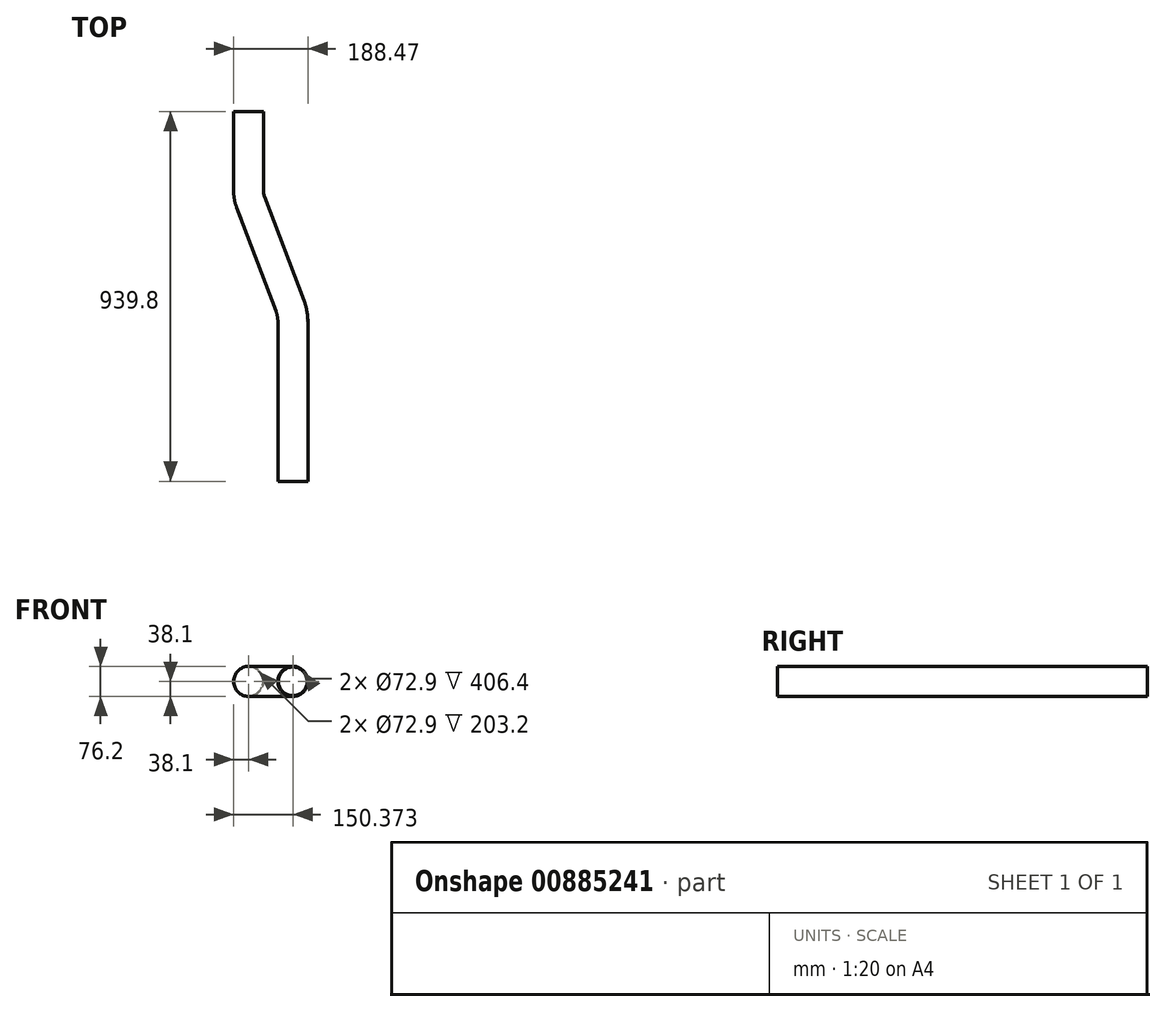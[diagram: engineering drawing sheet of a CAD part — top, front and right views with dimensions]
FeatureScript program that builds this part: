
annotation { "Feature Type Name" : "Feature", "Feature Type Description" : "" }
export const myFeature = defineFeature(function(context is Context, id is Id, definition is map)
    precondition{}
    {
        {
            var Q0;
            Q0=qCreatedBy(makeId("Front.planeOp"),FACE);
            var sketch = newSketch(context, id + "F0", { "sketchPlane" : qUnion([Q0])});
            skCircle(sketch, "E0", {"center": v(0, 0) * mm, "radius": 38.1 * mm});
            skCircle(sketch, "E1", {"center": v(0, 0) * mm, "radius": 36.45 * mm});
            skSolve(sketch);
        }
        {
            var Q0;
            Q0=qCreatedBy(makeId("Top.planeOp"),FACE);
            var sketch = newSketch(context, id + "F1", { "sketchPlane" : qUnion([Q0])});
            skLineSegment(sketch, "E2", {"start": v(0, 0) * mm, "end": v(0, -203.2) * mm});
            skArc(sketch, "E3", {"start": v(0, -203.2) * mm, "mid": v(1.25, -216.95) * mm, "end": v(4.96, -230.25) * mm});
            skArc(sketch, "E4", {"start": v(112.27, -533.4) * mm, "mid": v(110.43, -513.14) * mm, "end": v(104.96, -493.54) * mm});
            skLineSegment(sketch, "E5", {"start": v(104.96, -493.54) * mm, "end": v(4.96, -230.25) * mm});
            skLineSegment(sketch, "E6", {"start": v(112.27, -533.4) * mm, "end": v(112.27, -939.8) * mm});
            skSolve(sketch);
        }
        {
            var Q0;
            Q0=makeQuery(id+"F0.imprint","IMPRINT",FACE,{"disambiguationData":[TD([[makeQuery(id+"F0.imprint","IMPRINT",EDGE,{"derivedFrom":sQuery(id+"F0.wireOp",EDGE,"E0")}),1.0]])]});
            var Q1;
            Q1=sQuery(id+"F1.wireOp",EDGE,"E2");
            var Q2;
            Q2=sQuery(id+"F1.wireOp",EDGE,"E3");
            var Q3;
            Q3=sQuery(id+"F1.wireOp",EDGE,"E5");
            var Q4;
            Q4=sQuery(id+"F1.wireOp",EDGE,"E4");
            var Q5;
            Q5=sQuery(id+"F1.wireOp",EDGE,"E6");
            sweep(context, id + "F2", {"profiles" : qUnion([Q0]), "path" : qUnion([Q1, Q2, Q3, Q4, Q5])});
        }
    });
